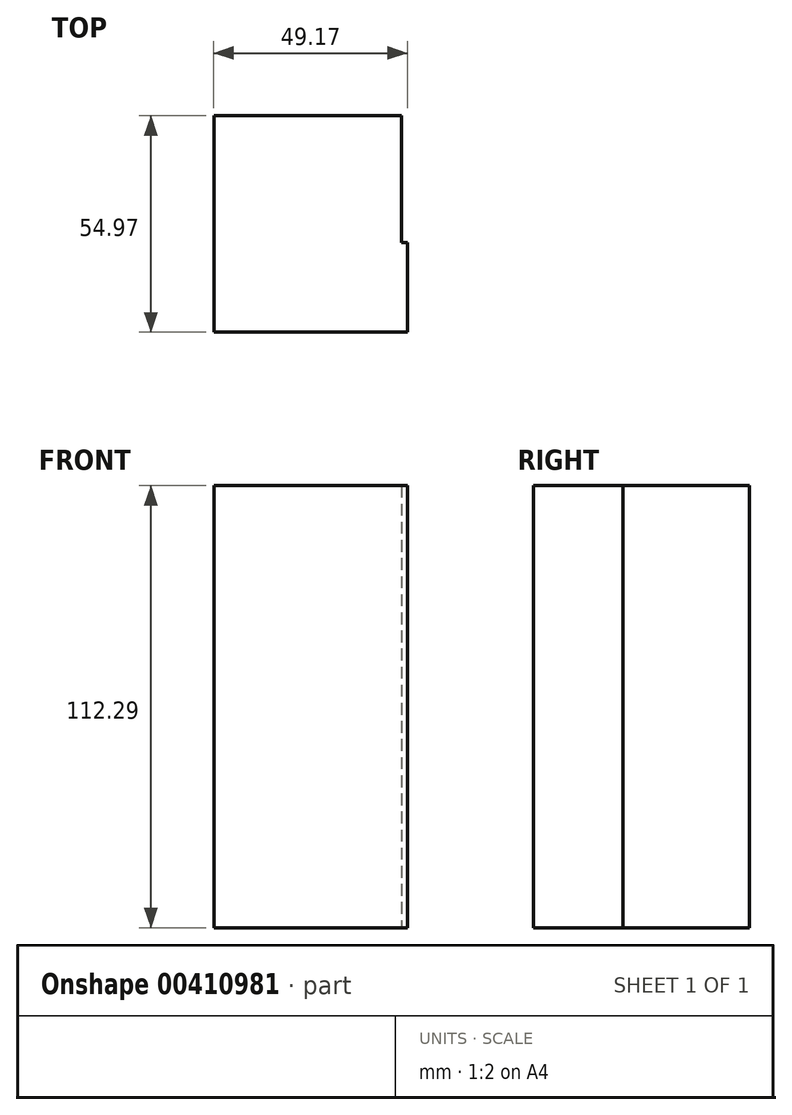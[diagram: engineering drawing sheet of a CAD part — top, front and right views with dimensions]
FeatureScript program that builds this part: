
annotation { "Feature Type Name" : "Feature", "Feature Type Description" : "" }
export const myFeature = defineFeature(function(context is Context, id is Id, definition is map)
    precondition{}
    {
        {
            var Q0;
            Q0=qCreatedBy(makeId("Top.planeOp"),FACE);
            var sketch = newSketch(context, id + "F0", { "sketchPlane" : qUnion([Q0])});
            skLineSegment(sketch, "E0.bottom", {"start": v(-8.5, 13.28) * mm, "end": v(39.2, 13.28) * mm});
            skLineSegment(sketch, "E0.top", {"start": v(-8.5, 45.43) * mm, "end": v(39.2, 45.43) * mm});
            skLineSegment(sketch, "E0.left", {"start": v(-8.5, 13.28) * mm, "end": v(-8.5, 45.43) * mm});
            skLineSegment(sketch, "E0.right", {"start": v(39.2, 13.28) * mm, "end": v(39.2, 45.43) * mm});
            skLineSegment(sketch, "E1.bottom", {"start": v(40.66, -9.54) * mm, "end": v(-8.5, -9.54) * mm});
            skLineSegment(sketch, "E1.top", {"start": v(40.66, 13.28) * mm, "end": v(-8.5, 13.28) * mm});
            skLineSegment(sketch, "E1.left", {"start": v(40.66, -9.54) * mm, "end": v(40.66, 13.28) * mm});
            skLineSegment(sketch, "E1.right", {"start": v(-8.5, -9.54) * mm, "end": v(-8.5, 13.28) * mm});
            skSolve(sketch);
        }
        {
            var Q0;
            Q0 = qSketchRegion(id + "F0", true);
            extrude(context, id + "F1", {"entities" : qUnion([Q0]), "depth" : 112.3 * mm});
        }
    });
